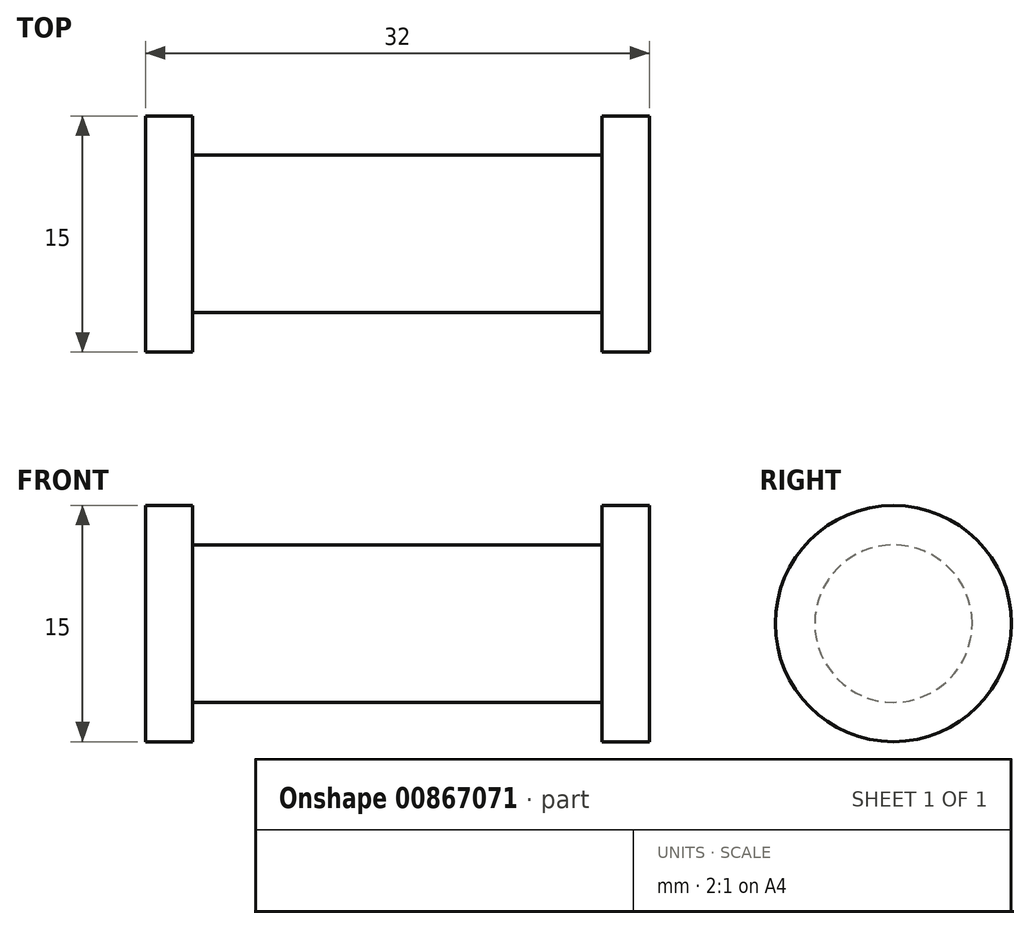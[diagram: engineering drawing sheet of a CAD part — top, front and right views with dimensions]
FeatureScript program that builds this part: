
annotation { "Feature Type Name" : "Feature", "Feature Type Description" : "" }
export const myFeature = defineFeature(function(context is Context, id is Id, definition is map)
    precondition{}
    {
        {
            var Q0;
            Q0=qCreatedBy(makeId("Top.planeOp"),FACE);
            var sketch = newSketch(context, id + "F0", { "sketchPlane" : qUnion([Q0])});
            skLineSegment(sketch, "E0.bottom", {"start": v(-13, 5) * mm, "end": v(13, 5) * mm});
            skLineSegment(sketch, "E0.top", {"start": v(-13, -5) * mm, "end": v(13, -5) * mm});
            skLineSegment(sketch, "E0.left", {"start": v(-13, 5) * mm, "end": v(-13, -5) * mm});
            skLineSegment(sketch, "E0.right", {"start": v(13, 5) * mm, "end": v(13, -5) * mm});
            skPoint(sketch, "E0.middle", {"position": v(0, 0) * mm});
            skPoint(sketch, "E1.middle", {"position": v(-13, 0) * mm});
            skLineSegment(sketch, "E2", {"start": v(-9.8, -5) * mm, "end": v(-13, -5) * mm});
            skPoint(sketch, "E3", {"position": v(13, 0) * mm});
            skLineSegment(sketch, "E4.bottom", {"start": v(-13, 7.5) * mm, "end": v(-16, 7.5) * mm});
            skLineSegment(sketch, "E4.top", {"start": v(-13, -7.5) * mm, "end": v(-16, -7.5) * mm});
            skLineSegment(sketch, "E4.left", {"start": v(-13, -7.5) * mm, "end": v(-13, 7.5) * mm});
            skLineSegment(sketch, "E4.right", {"start": v(-16, -7.5) * mm, "end": v(-16, 7.5) * mm});
            skPoint(sketch, "E4.middle", {"position": v(-14.5, 0) * mm});
            skLineSegment(sketch, "E5.bottom", {"start": v(16, -7.5) * mm, "end": v(13, -7.5) * mm});
            skLineSegment(sketch, "E5.top", {"start": v(16, 7.5) * mm, "end": v(13, 7.5) * mm});
            skLineSegment(sketch, "E5.left", {"start": v(16, -7.5) * mm, "end": v(16, 7.5) * mm});
            skLineSegment(sketch, "E5.right", {"start": v(13, -7.5) * mm, "end": v(13, 7.5) * mm});
            skPoint(sketch, "E5.middle", {"position": v(14.5, 0) * mm});
            skLineSegment(sketch, "E6", {"start": v(-16, 0) * mm, "end": v(16, 0) * mm});
            skSolve(sketch);
        }
        {
            var Q0;
            {var subQ1=sQuery(id+"F0.wireOp",EDGE,"E4.bottom");Q0=makeQuery(id+"F0.imprint","IMPRINT",FACE,{"disambiguationData":[TD([[makeQuery(id+"F0.imprint","IMPRINT",EDGE,{"derivedFrom":subQ1}),1.0]])]});}
            var Q1;
            {var subQ0=sQuery(id+"F0.wireOp",EDGE,"E0.bottom");Q1=makeQuery(id+"F0.imprint","IMPRINT",FACE,{"disambiguationData":[TD([[makeQuery(id+"F0.imprint","IMPRINT",EDGE,{"derivedFrom":subQ0}),-1.0]])]});}
            var Q2;
            {var subQ2=sQuery(id+"F0.wireOp",EDGE,"E5.top");Q2=makeQuery(id+"F0.imprint","IMPRINT",FACE,{"disambiguationData":[TD([[makeQuery(id+"F0.imprint","IMPRINT",EDGE,{"derivedFrom":subQ2}),1.0]])]});}
            var Q3;
            Q3=sQuery(id+"F0.wireOp",EDGE,"E6");
            revolve(context, id + "F1", {"surfaceOperationType" : NewSurfaceOperationType.NEW, "entities" : qUnion([Q0, Q1, Q2]), "axis" : qUnion([Q3]), "revolveType" : RevolveType.FULL});
        }
    });
